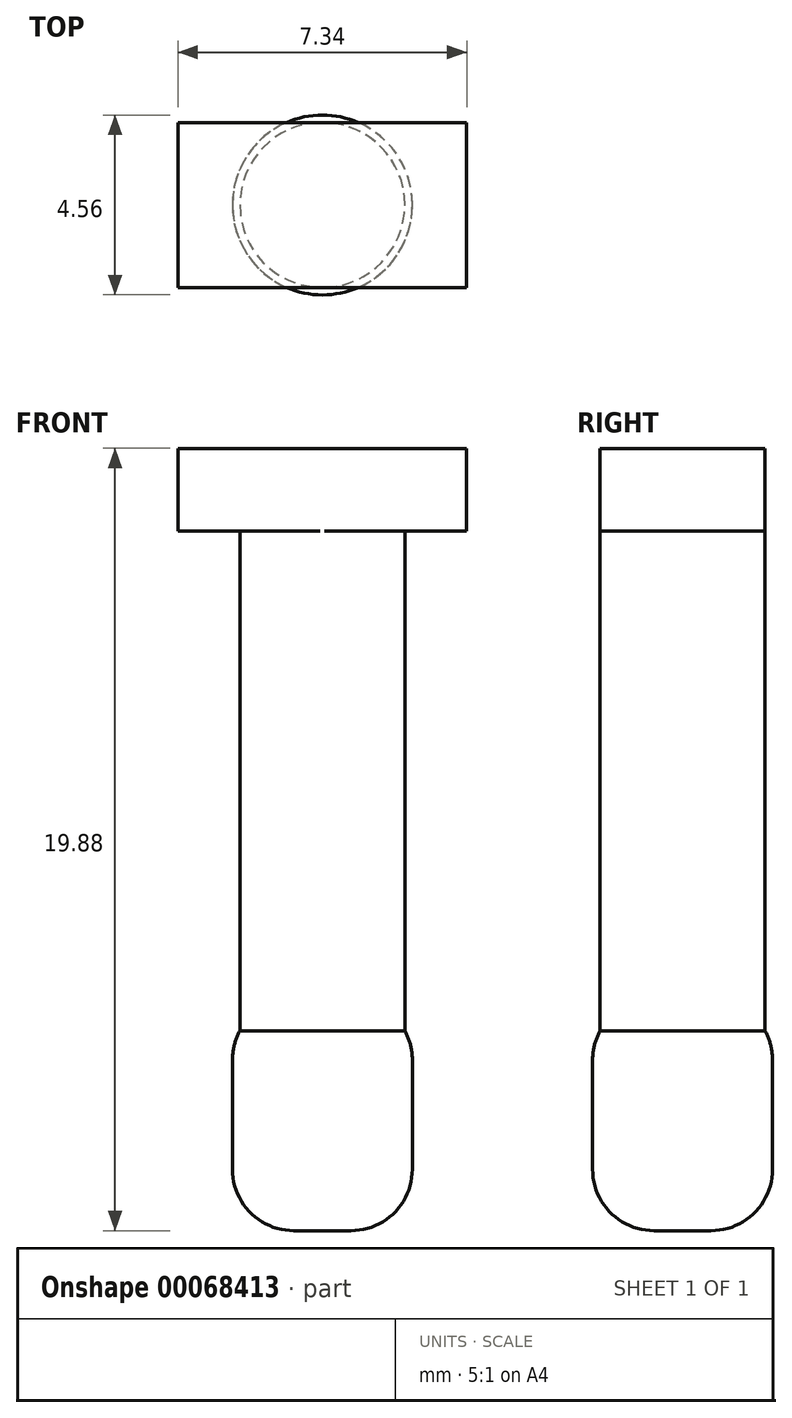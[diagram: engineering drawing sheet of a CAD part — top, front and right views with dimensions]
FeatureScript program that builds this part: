
annotation { "Feature Type Name" : "Feature", "Feature Type Description" : "" }
export const myFeature = defineFeature(function(context is Context, id is Id, definition is map)
    precondition{}
    {
        {
            var Q0;
            Q0=qCreatedBy(makeId("Top.planeOp"),FACE);
            var sketch = newSketch(context, id + "F0", { "sketchPlane" : qUnion([Q0])});
            skCircle(sketch, "E0", {"center": v(0, 0) * mm, "radius": 2.1 * mm});
            skSolve(sketch);
        }
        {
            var Q0;
            Q0 = qSketchRegion(id + "F0", true);
            extrude(context, id + "F1", {"entities" : qUnion([Q0]), "depth" : 12.7 * mm});
        }
        {
            var Q0;
            Q0=makeQuery(id+"F1.opExtrude","CAP_FACE",FACE,{"disambiguationData":[OSD([sQuery(id+"F0.wireOp",EDGE,"E0")])],"isStart":false});
            var sketch = newSketch(context, id + "F2", { "sketchPlane" : qUnion([Q0])});
            skLineSegment(sketch, "E1.bottom", {"start": v(3.67, -2.1) * mm, "end": v(-3.67, -2.1) * mm});
            skLineSegment(sketch, "E1.top", {"start": v(3.67, 2.1) * mm, "end": v(-3.67, 2.1) * mm});
            skLineSegment(sketch, "E1.left", {"start": v(3.67, -2.1) * mm, "end": v(3.67, 2.1) * mm});
            skLineSegment(sketch, "E1.right", {"start": v(-3.67, -2.1) * mm, "end": v(-3.67, 2.1) * mm});
            skPoint(sketch, "E1.middle", {"position": v(0, 0) * mm});
            skSolve(sketch);
        }
        {
            var Q0;
            Q0 = qSketchRegion(id + "F2", true);
            extrude(context, id + "F3", {"entities" : qUnion([Q0]), "operationType" : NewBodyOperationType.ADD, "depth" : 2.1 * mm});
        }
        {
            var Q0;
            Q0=makeQuery(id+"F1.opExtrude","CAP_FACE",FACE,{"disambiguationData":[OSD([sQuery(id+"F0.wireOp",EDGE,"E0")])],"isStart":true});
            var sketch = newSketch(context, id + "F4", { "sketchPlane" : qUnion([Q0])});
            skCircle(sketch, "E2", {"center": v(0, 0) * mm, "radius": 2.28 * mm});
            skSolve(sketch);
        }
        {
            var Q0;
            Q0=makeQuery(id+"F4.imprint","IMPRINT",FACE,{"disambiguationData":[TD([[makeQuery(id+"F4.imprint","IMPRINT",EDGE,{"derivedFrom":makeQuery(id+"F1.opExtrude","CAP_EDGE",EDGE,{"disambiguationData":[OSD([sQuery(id+"F0.wireOp",EDGE,"E0")])],"isStart":true})}),-1.0]])]});
            var Q1;
            Q1=makeQuery(id+"F4.imprint","IMPRINT",FACE,{"disambiguationData":[TD([[makeQuery(id+"F4.imprint","IMPRINT",EDGE,{"derivedFrom":sQuery(id+"F4.wireOp",EDGE,"E2")}),1.0]])]});
            extrude(context, id + "F5", {"entities" : qUnion([Q0, Q1]), "operationType" : NewBodyOperationType.ADD, "depth" : 5.08 * mm});
        }
        {
            var Q0;
            Q0=makeQuery(id+"F5.opExtrude","CAP_EDGE",EDGE,{"disambiguationData":[OSD([sQuery(id+"F4.wireOp",EDGE,"E2")])],"isStart":true});
            var Q1;
            Q1=makeQuery(id+"F5.opExtrude","CAP_EDGE",EDGE,{"disambiguationData":[OSD([sQuery(id+"F4.wireOp",EDGE,"E2")])],"isStart":false});
            fillet(context, id + "F6", {"entities" : qUnion([Q0, Q1]), "radius" : 1.56 * mm, "tangentPropagation" : true, "allowEdgeOverflow" : false});
        }
    });
